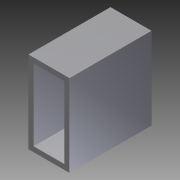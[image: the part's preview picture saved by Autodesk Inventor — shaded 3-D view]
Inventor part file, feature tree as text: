
AUTODESK INVENTOR PART (.ipt)
format: ipt  version: 2012 (Build 160160000, 160)  size: 77,824 bytes
history: native  units: in
note: dims shown in document units (in); Inventor stores cm internally (conversion verified against a paired STEP export)
features: extrude x1, sketch x1
ambient origin geometry x8: Origin, YZ Plane, XZ Plane, XY Plane, X Axis, Y Axis, Z Axis, Center Point
bodies: Solid1 (feature_tree)
feature tree (2):
  extrude  "Extrusion1"  Depth=0.125in
  sketch  "Sketch1"  dims[d0=0.125in d1=0.125in d2=0.125in d3=0.125in d4=2.0in d5=1.0in d6=2.0in d7=0.0in]
